# Revit family: Shower-Shower_Door-KOHLER-Revel-K-707510_1
name_source: partatom
category: Specialty Equipment
units: mm (PartAtom-declared; Revit-internal decimal feet)

## family parameters
Cut with Voids When Loaded = No
Host = Face
Maintain Annotation Orientation = No
OmniClass Number = 23.31.17.17
OmniClass Title = Shower Enclosures
Part Type = Normal
Room Calculation Point = No
Round Connector Dimension = Use Diameter
Shared = No

## types (6) — shared parameters
ADA Compliant = No
Assembly Code = C1030200
Date Modified = 06/17/2022
Default Elevation = 4"
Height = 70"
Length = 4 1/8"
Manufacturer = Kohler Co.
Master Format 2014 = 10 28 19.16
Master Format 2014 Name = Shower Doors
Material = Premium Metal Construction
Product Documentation Link = https://www.us.kohler.com
Product Name = Revel
Product Page URL = http://www.us.kohler.com
URL = https://www.us.kohler.com
WaterSense Certified = No

## per-type parameters (varying)
| type | Description | Finish | Handle Finish | Model | Secondary Finish | Type |
| Clear Glass, ABZ-Anodized Dark Bronze | Pivot shower door, 70 inch H x 31-1/8 - 36 inch W, with 1/4 inch thick Crystal Clear glass | Kohler-Metal-ABZ-Anodized_Dark_Bronze | Kohler-Metal-BL-Matte_Black | K-707510-L-ABZ | Kohler-Glass-L-Crystal_Clear | 1 |
| Clear Glass, BNK-Anodized Brushed Nickel | Pivot shower door, 70 inch H x 31-1/8 - 36 inch W, with 1/4 inch thick Crystal Clear glass | Kohler-Metal-BNK-Anodized_Brushed_Nickel | Kohler-Metal-BN-Vibrant_Brushed_Nickel | K-707510-L-BNK | Kohler-Glass-L-Crystal_Clear | 2 |
| Clear Glass, SHP-Bright Polished Silver | Pivot shower door, 70 inch H x 31-1/8 - 36 inch W, with 1/4 inch thick Crystal Clear glass | Kohler-Metal-SHP-Bright_Polished_Silver | Kohler-Metal-CP-Polished_Chrome | K-707510-L-SHP | Kohler-Glass-L-Crystal_Clear | 3 |
| Frosted Glass, ABZ-Anodized Dark Bronze | Pivot shower door, 70 inch H x 31-1/8 - 36 inch W, with 1/4 inch thick Frosted glass | Kohler-Metal-ABZ-Anodized_Dark_Bronze | Kohler-Metal-BL-Matte_Black | K-707510-D3-ABZ | KOHLER-Frosted_Glass | 4 |
| Frosted Glass, BNK-Anodized Brushed Nickel | Pivot shower door, 70 inch H x 31-1/8 - 36 inch W, with 1/4 inch thick Frosted glass | Kohler-Metal-BNK-Anodized_Brushed_Nickel | Kohler-Metal-BN-Vibrant_Brushed_Nickel | K-707510-D3-BNK | KOHLER-Frosted_Glass | 5 |
| Frosted Glass, SHP-Bright Polished Silver | Pivot shower door, 70 inch H x 31-1/8 - 36 inch W, with 1/4 inch thick Frosted glass | Kohler-Metal-SHP-Bright_Polished_Silver | Kohler-Metal-CP-Polished_Chrome | K-707510-D3-SHP | KOHLER-Frosted_Glass | 6 |

## geometry (parser evidence)
native form markers: Sweep x4
no freeform markers — native parametric forms only
